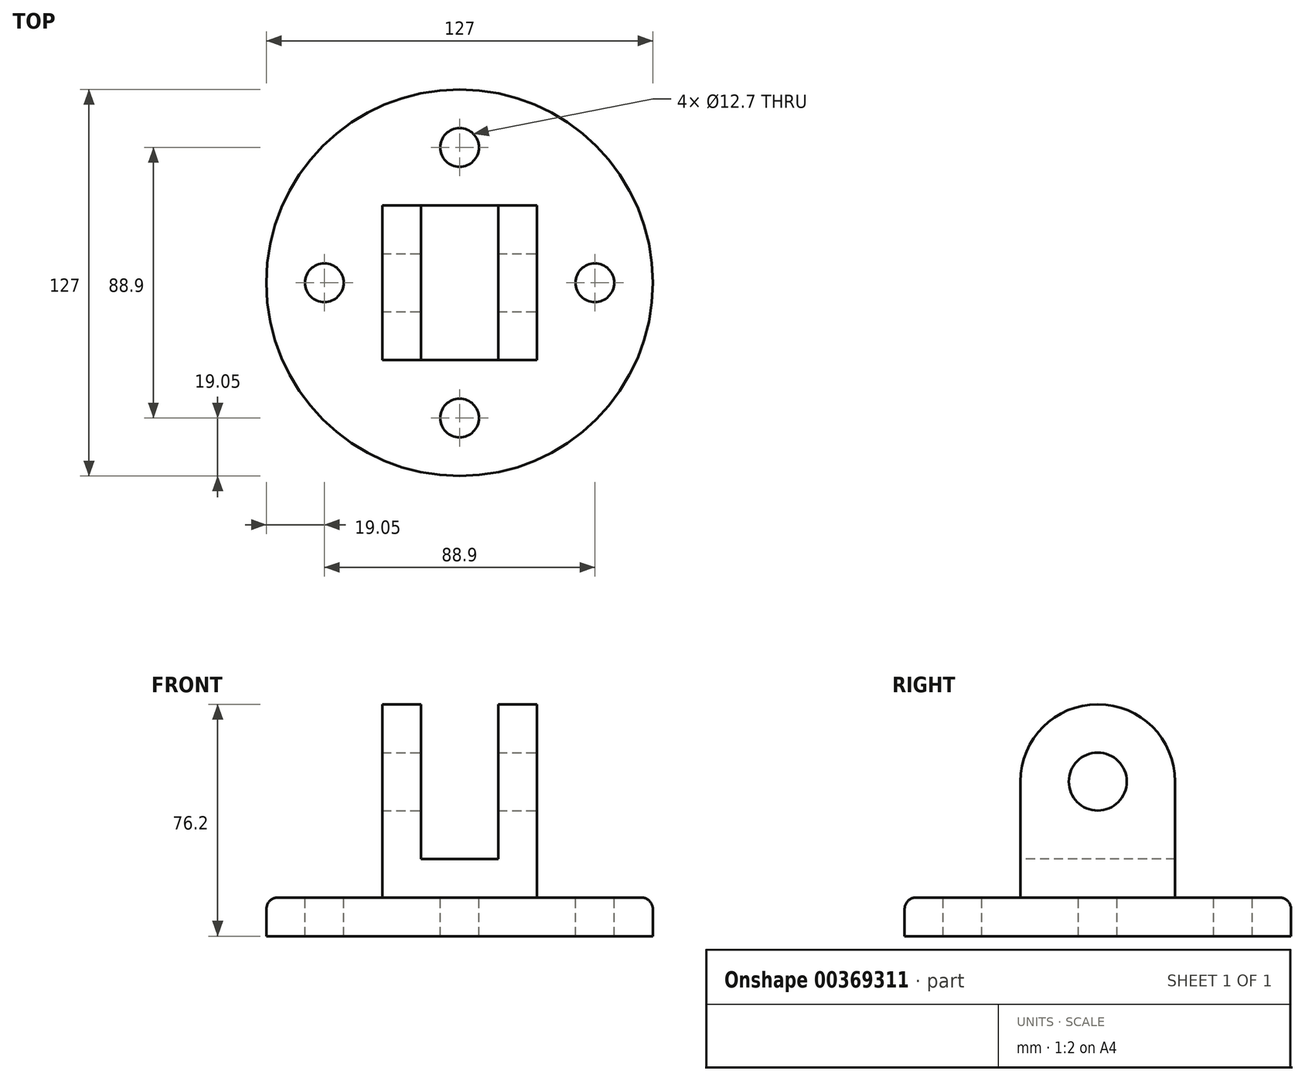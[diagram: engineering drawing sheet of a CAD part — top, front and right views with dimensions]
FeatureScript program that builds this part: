
annotation { "Feature Type Name" : "Feature", "Feature Type Description" : "" }
export const myFeature = defineFeature(function(context is Context, id is Id, definition is map)
    precondition{}
    {
        {
            var Q0;
            Q0=qCreatedBy(makeId("Top.planeOp"),FACE);
            var sketch = newSketch(context, id + "F0", { "sketchPlane" : qUnion([Q0])});
            skCircle(sketch, "E0", {"center": v(0, 0) * mm, "radius": 63.5 * mm});
            skSolve(sketch);
        }
        {
            var Q0;
            Q0 = qSketchRegion(id + "F0", true);
            extrude(context, id + "F1", {"entities" : qUnion([Q0]), "depth" : 12.7 * mm});
        }
        {
            var Q0;
            Q0=qCreatedBy(makeId("Right.planeOp"),FACE);
            var sketch = newSketch(context, id + "F2", { "sketchPlane" : qUnion([Q0])});
            skLineSegment(sketch, "E1", {"start": v(0, 0) * mm, "end": v(0, 12.7) * mm, "construction": true});
            skLineSegment(sketch, "E2", {"start": v(-25.4, 12.7) * mm, "end": v(25.4, 12.7) * mm});
            skLineSegment(sketch, "E3", {"start": v(25.4, 12.7) * mm, "end": v(25.4, 50.8) * mm});
            skLineSegment(sketch, "E4", {"start": v(25.4, 50.8) * mm, "end": v(-25.4, 50.8) * mm});
            skLineSegment(sketch, "E5", {"start": v(-25.4, 50.8) * mm, "end": v(-25.4, 12.7) * mm});
            skSolve(sketch);
        }
        {
            var Q0;
            Q0 = qSketchRegion(id + "F2", true);
            extrude(context, id + "F3", {"entities" : qUnion([Q0]), "operationType" : NewBodyOperationType.ADD, "endBound" : BoundingType.SYMMETRIC, "depth" : 50.8 * mm});
        }
        {
            var Q0;
            Q0=qCreatedBy(makeId("Right.planeOp"),FACE);
            var sketch = newSketch(context, id + "F4", { "sketchPlane" : qUnion([Q0])});
            skLineSegment(sketch, "E6.0", {"start": v(25.4, 50.8) * mm, "end": v(-25.4, 50.8) * mm});
            skArc(sketch, "E7", {"start": v(25.4, 50.8) * mm, "mid": v(0, 76.2) * mm, "end": v(-25.4, 50.8) * mm});
            skSolve(sketch);
        }
        {
            var Q0;
            Q0 = qSketchRegion(id + "F4", true);
            extrude(context, id + "F5", {"entities" : qUnion([Q0]), "operationType" : NewBodyOperationType.ADD, "endBound" : BoundingType.SYMMETRIC, "depth" : 50.8 * mm});
        }
        {
            var Q0;
            Q0=makeQuery(id+"F5.boolean.opBoolean","MERGE",FACE,{"derivedFrom":[makeQuery(id+"F3.opExtrude","CAP_FACE",FACE,{"disambiguationData":[OSD([sQuery(id+"F2.wireOp",EDGE,"E2"),sQuery(id+"F2.wireOp",EDGE,"E3"),sQuery(id+"F2.wireOp",EDGE,"E4"),sQuery(id+"F2.wireOp",EDGE,"E5")])],"isStart":false}),makeQuery(id+"F5.opExtrude","CAP_FACE",FACE,{"disambiguationData":[OSD([sQuery(id+"F4.wireOp",EDGE,"E6.0"),sQuery(id+"F4.wireOp",EDGE,"E7")])],"isStart":false})]});
            var sketch = newSketch(context, id + "F6", { "sketchPlane" : qUnion([Q0])});
            skCircle(sketch, "E8", {"center": v(0, 50.8) * mm, "radius": 9.53 * mm});
            skSolve(sketch);
        }
        {
            var Q0;
            Q0 = qSketchRegion(id + "F6", true);
            extrude(context, id + "F7", {"entities" : qUnion([Q0]), "operationType" : NewBodyOperationType.REMOVE, "endBound" : BoundingType.THROUGH_ALL, "oppositeDirection" : true, "depth" : 25.4 * mm});
        }
        {
            var Q0;
            Q0=qCreatedBy(makeId("Front.planeOp"),FACE);
            var sketch = newSketch(context, id + "F8", { "sketchPlane" : qUnion([Q0])});
            skLineSegment(sketch, "E9", {"start": v(0, 0) * mm, "end": v(0, 25.4) * mm, "construction": true});
            skLineSegment(sketch, "E10", {"start": v(-12.7, 25.4) * mm, "end": v(12.7, 25.4) * mm});
            skLineSegment(sketch, "E11", {"start": v(-12.7, 25.4) * mm, "end": v(-12.7, 76.2) * mm});
            skLineSegment(sketch, "E12", {"start": v(-12.7, 76.2) * mm, "end": v(12.7, 76.2) * mm});
            skLineSegment(sketch, "E13", {"start": v(12.7, 76.2) * mm, "end": v(12.7, 25.4) * mm});
            skSolve(sketch);
        }
        {
            var Q0;
            Q0 = qSketchRegion(id + "F8", true);
            extrude(context, id + "F9", {"entities" : qUnion([Q0]), "operationType" : NewBodyOperationType.REMOVE, "endBound" : BoundingType.THROUGH_ALL, "oppositeDirection" : true, "depth" : 25.4 * mm, "hasSecondDirection" : true, "secondDirectionOppositeDirection" : false, "secondDirectionDepth" : 25.4 * mm});
        }
        {
            var Q0;
            Q0=makeQuery(id+"F1.opExtrude","CAP_FACE",FACE,{"disambiguationData":[OSD([sQuery(id+"F0.wireOp",EDGE,"E0")])],"isStart":false});
            var sketch = newSketch(context, id + "F10", { "sketchPlane" : qUnion([Q0])});
            skCircle(sketch, "E14", {"center": v(0, 44.45) * mm, "radius": 6.35 * mm});
            skCircle(sketch, "E15", {"center": v(-44.45, 0) * mm, "radius": 6.35 * mm});
            skCircle(sketch, "E16", {"center": v(0, -44.45) * mm, "radius": 6.35 * mm});
            skCircle(sketch, "E17", {"center": v(44.45, 0) * mm, "radius": 6.35 * mm});
            skCircle(sketch, "E18", {"center": v(0, 0) * mm, "radius": 44.45 * mm, "construction": true});
            skSolve(sketch);
        }
        {
            var Q0;
            Q0 = qSketchRegion(id + "F10", true);
            extrude(context, id + "F11", {"entities" : qUnion([Q0]), "operationType" : NewBodyOperationType.REMOVE, "endBound" : BoundingType.THROUGH_ALL, "oppositeDirection" : true, "depth" : 25.4 * mm});
        }
        {
            var Q0;
            Q0=makeQuery(id+"F3.opExtrude","SWEPT_EDGE",EDGE,{"disambiguationData":[OSD([sQuery(id+"F2.wireOp",EDGE,"E2"),sQuery(id+"F2.wireOp",EDGE,"E3")])]});
            var Q1;
            Q1=makeQuery(id+"F3.opExtrude","CAP_EDGE",EDGE,{"disambiguationData":[OSD([sQuery(id+"F2.wireOp",EDGE,"E2")])],"isStart":false});
            var Q2;
            Q2=makeQuery(id+"F3.opExtrude","CAP_EDGE",EDGE,{"disambiguationData":[OSD([sQuery(id+"F2.wireOp",EDGE,"E2")])],"isStart":true});
            var Q3;
            Q3=makeQuery(id+"F3.opExtrude","SWEPT_EDGE",EDGE,{"disambiguationData":[OSD([sQuery(id+"F2.wireOp",EDGE,"E2"),sQuery(id+"F2.wireOp",EDGE,"E5")])]});
            var Q4;
            Q4=makeQuery(id+"F1.opExtrude","CAP_EDGE",EDGE,{"disambiguationData":[OSD([sQuery(id+"F0.wireOp",EDGE,"E0")])],"isStart":false});
            fillet(context, id + "F12", {"entities" : qUnion([Q0, Q1, Q2, Q3, Q4]), "radius" : 3.8 * mm, "tangentPropagation" : true, "allowEdgeOverflow" : false});
        }
    });
